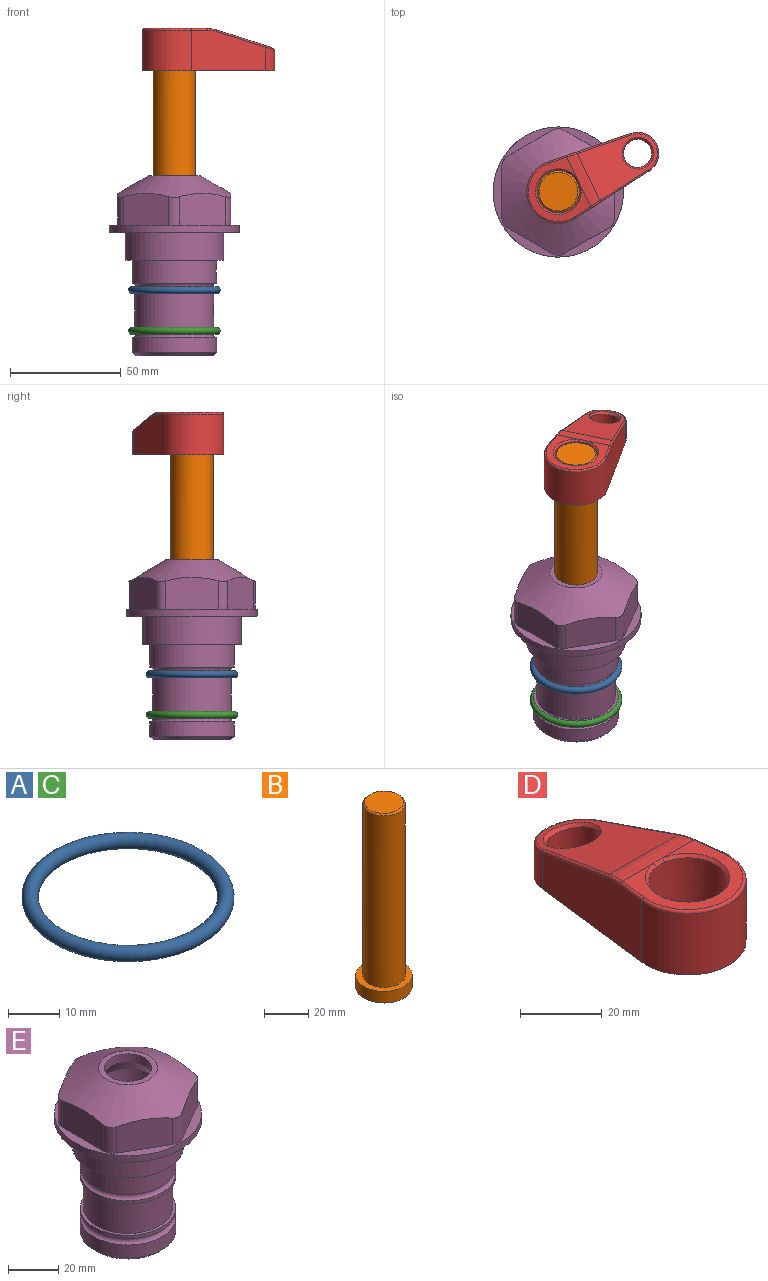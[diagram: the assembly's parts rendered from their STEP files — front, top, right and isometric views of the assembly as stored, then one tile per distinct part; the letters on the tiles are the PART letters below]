
ASSEMBLY  parts=5 mates=4
PART A: 1 faces, bbox 44.7x44.7x3.2 mm
  f0: torus R=19.05mm, axis (0,0,1), area 1193.9mm2
PART B: 6 faces, bbox 25.4x25.4x101.6 mm
  f0: plane 17.46x17.46mm, normal (0,0,1), area 239.5mm2, adj f5
  f1: plane 25.4x25.4mm, normal (0,0,-1), area 506.7mm2, adj f2
  f2: cylinder r=12.7mm len=25.4mm, axis (0,0,1), area 506.7mm2, adj f1,f3
  f3: plane 25.4x25.4mm, normal (0,0,1), area 221.7mm2, adj f2,f4
  f4: cylinder r=9.53mm len=94.46mm, axis (0,0,1), area 5653mm2, adj f3,f5
  f5: cone r=8.73mm half-angle=45deg, axis (0,0,-1), area 64.4mm2, adj f0,f4
PART C: same geometry as A
PART D: 31 faces, bbox 31.7x65.5x19.8 mm
  f0: plane 39.12x18.26mm, normal (0.99,0.12,0), area 612.2mm2, adj f1,f4,f7,f11,f13,f15
  f1: cylinder r=9.53mm len=18.91mm, axis (0,0,-1), area 296.1mm2, adj f0,f2,f7,f17
  f2: plane 39.12x18.26mm, normal (-0.99,0.12,0), area 612.2mm2, adj f1,f4,f7,f12,f14,f16
  f3: cylinder r=6.35mm len=12.7mm, axis (0,0,-1), area 362.4mm2, adj f7,f18
  f4: cylinder r=14.29mm len=28.58mm, axis (0,0,-1), area 882.2mm2, adj f0,f2,f7,f10
  f5: cylinder r=9.53mm len=19.05mm, axis (0,0,-1), area 1092.6mm2, adj f7,f19,f20
  f6: plane 26.99x23.69mm, normal (0,0,1), area 216.2mm2, adj f9,f10,f11,f12,f19
  f7: plane 63.5x28.58mm, normal (0,0,-1), area 661.8mm2, adj f0,f1,f2,f3,f4,f5,f22,f23
  f8: plane 33.52x23.6mm, normal (0,0.26,0.97), area 486mm2, adj f9,f15,f16,f17,f18
  f9: cylinder r=19.05mm len=24.72mm, axis (1,0,0), area 120.4mm2, adj f6,f8,f13,f14,f20
  f10: torus R=13.49mm, axis (0,0,1), area 59mm2, adj f4,f6,f11,f12
  f11: cylinder r=0.79mm len=8.67mm, axis (0.12,-0.99,0), area 10.8mm2, adj f0,f6,f10,f13
  f12: cylinder r=0.79mm len=8.67mm, axis (0.12,0.99,0), area 10.8mm2, adj f2,f6,f10,f14
  f13: bspline ~4.95x1.42mm, area 6.1mm2, adj f0,f9,f11,f15
  f14: bspline ~4.95x1.42mm, area 6.1mm2, adj f2,f9,f12,f16
  f15: cylinder r=0.79mm len=25.95mm, axis (0.12,-0.96,0.26), area 32.9mm2, adj f0,f8,f13,f17
  f16: cylinder r=0.79mm len=25.95mm, axis (0.12,0.96,-0.26), area 32.9mm2, adj f2,f8,f14,f17
  f17: bspline ~18.91x8.38mm, area 30mm2, adj f1,f8,f15,f16
  f18: bspline ~14.29x14.29mm, area 48.3mm2, adj f3,f8
  f19: cone r=9.53mm half-angle=45deg, axis (0,0,1), area 66.5mm2, adj f5,f6,f20
  f20: bspline ~3.22x0.96mm, area 3.5mm2, adj f5,f9,f19
  f21: plane 2.75x2.72mm, normal (0,0,-1), area 2.9mm2, adj f23,f25,f28
  f22: plane 23.05x15.88mm, normal (-0.99,-0.12,0), area 323.6mm2, adj f7,f25,f26,f27,f28,f29
  f23: plane 23.05x15.88mm, normal (0.99,-0.12,0), area 323.6mm2, adj f7,f21,f25,f27,f28,f30
  f24: cylinder r=9.53mm len=10.69mm, axis (0,0,-1), area 114.7mm2, adj f7,f27,f29,f30
  f25: cylinder r=12.7mm len=20.59mm, axis (0,0,-1), area 381.1mm2, adj f7,f21,f22,f23,f26,f28
  f26: plane 2.75x2.72mm, normal (0,0,-1), area 2.9mm2, adj f22,f25,f28
  f27: plane 19.72x18.37mm, normal (0,-0.26,-0.97), area 291.8mm2, adj f22,f23,f24,f28,f29,f30
  f28: cylinder r=15.88mm len=19.92mm, axis (1,0,0), area 54.8mm2, adj f21,f22,f23,f25,f26,f27
  f29: cylinder r=1.59mm len=11mm, axis (0,0,-1), area 34.7mm2, adj f7,f22,f24,f27
  f30: cylinder r=1.59mm len=11mm, axis (0,0,-1), area 34.7mm2, adj f7,f23,f24,f27
PART E: 36 faces, bbox 58.7x58.7x81 mm
  f0: cylinder r=17.78mm len=35.56mm, axis (0,0,1), area 1670.8mm2, adj f23,f24,f31
  f1: cylinder r=19.05mm len=38.1mm, axis (0,0,1), area 1191.9mm2, adj f26,f27,f30
  f2: plane 58.66x58.66mm, normal (0,0,-1), area 1150.6mm2, adj f3,f28
  f3: cylinder r=29.33mm len=58.66mm, axis (0,0,-1), area 585.1mm2, adj f2,f4
  f4: plane 58.66x58.66mm, normal (0,0,1), area 475.9mm2, adj f3,f5,f6,f7,f8,f9,f10,f11
  f5: plane 20.32x14.34mm, normal (-0.5,0.87,0), area 324.4mm2, adj f4,f15,f16,f17
  f6: plane 20.32x14.34mm, normal (0.5,0.87,0), area 324.4mm2, adj f4,f14,f15,f17
  f7: plane 23.48x14.34mm, normal (1,0,0), area 324.4mm2, adj f4,f13,f14,f17
  f8: plane 20.32x14.34mm, normal (0.5,-0.87,0), area 324.4mm2, adj f4,f12,f13,f17
  f9: plane 20.32x14.34mm, normal (-0.5,-0.87,0), area 324.4mm2, adj f4,f11,f12,f17
  f10: plane 23.48x14.34mm, normal (-1,0,0), area 324.4mm2, adj f4,f11,f16,f17
  f11: cylinder r=5.08mm len=12.85mm, axis (0,0,-1), area 67.2mm2, adj f4,f9,f10,f17
  f12: cylinder r=5.08mm len=12.85mm, axis (0,0,-1), area 67.2mm2, adj f4,f8,f9,f17
  f13: cylinder r=5.08mm len=12.85mm, axis (0,0,-1), area 67.2mm2, adj f4,f7,f8,f17
  f14: cylinder r=5.08mm len=12.85mm, axis (0,0,-1), area 67.2mm2, adj f4,f6,f7,f17
  f15: cylinder r=5.08mm len=12.85mm, axis (0,0,-1), area 67.2mm2, adj f4,f5,f6,f17
  f16: cylinder r=5.08mm len=12.85mm, axis (0,0,-1), area 67.2mm2, adj f4,f5,f10,f17
  f17: cone r=11.73mm half-angle=60deg, axis (0,0,-1), area 2071.8mm2, adj f5,f6,f7,f8,f9,f10,f11,f12
  f18: plane 23.46x23.46mm, normal (0,0,1), area 147.4mm2, adj f17,f35
  f19: plane 34.93x34.93mm, normal (0,0,-1), area 958mm2, adj f29
  f20: cylinder r=19.05mm len=38.1mm, axis (0,0,1), area 760.1mm2, adj f21,f29
  f21: torus R=19.05mm, axis (0,0,1), area 565.3mm2, adj f20,f22
  f22: cylinder r=19.05mm len=38.1mm, axis (0,0,1), area 190mm2, adj f21,f23
  f23: plane 38.1x38.1mm, normal (0,0,1), area 146.9mm2, adj f0,f22
  f24: plane 38.1x38.1mm, normal (0,0,-1), area 146.9mm2, adj f0,f25
  f25: cylinder r=19.05mm len=38.1mm, axis (0,0,1), area 190mm2, adj f24,f26
  f26: torus R=19.05mm, axis (0,0,1), area 565.3mm2, adj f1,f25
  f27: plane 44.45x44.45mm, normal (0,0,-1), area 411.7mm2, adj f1,f28
  f28: cylinder r=22.23mm len=44.45mm, axis (0,0,1), area 1773.5mm2, adj f2,f27
  f29: cone r=19.05mm half-angle=45deg, axis (0,0,1), area 257.5mm2, adj f19,f20
  f30: cylinder r=3.17mm len=6.75mm, axis (-1,0,0), area 128mm2, adj f1,f33
  f31: cylinder r=3.17mm len=6.35mm, axis (-1,0,0), area 102.5mm2, adj f0,f33
  f32: plane 25.4x25.4mm, normal (0,0,1), area 506.7mm2, adj f33
  f33: cylinder r=12.7mm len=66.42mm, axis (0,0,-1), area 5236.2mm2, adj f30,f31,f32,f34
  f34: cone r=9.53mm half-angle=30deg, axis (0,0,-1), area 443.4mm2, adj f33,f35
  f35: cylinder r=9.53mm len=19.05mm, axis (0,0,-1), area 240.9mm2, adj f18,f34
PLACE A t=(0,0,-1.59)mm
PLACE B rot(axis=(0,0,-1),64.2deg) t=(0,0,27.55)mm
PLACE C t=(0,0,-20)mm
PLACE D rot(axis=(0,0,-1),64.2deg) t=(0,0,28.35)mm
PLACE E at identity fixed
MATE fastened B.f2 <-> D.f4  axis (0,0,1) through (0,0,91.05)mm
MATE fastened C.f0 <-> E.f0  axis (0,0,1) through (0,0,-44.51)mm
MATE cylindrical B.f2 <-> E.f0  axis (0,0,-1) through (0,0,-10.55)mm
MATE fastened A.f0 <-> E.f0  axis (0,0,1) through (0,0,-26.1)mm
